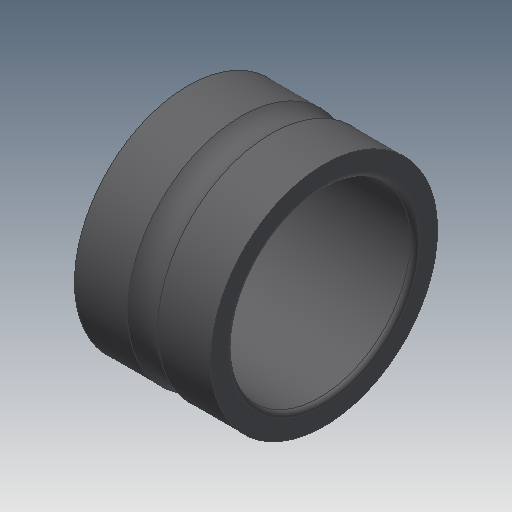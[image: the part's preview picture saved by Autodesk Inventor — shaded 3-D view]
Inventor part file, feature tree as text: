
AUTODESK INVENTOR PART (.ipt)
format: ipt  version: 2019.4 (Build 234330000, 330)  size: 198,656 bytes
history: native  units: mm
features: other x98, revolve x1, sketch x1
ambient origin geometry x8: Origin, YZ Plane, XZ Plane, XY Plane, X Axis, Y Axis, Z Axis, Center Point
bodies: Solid1 (feature_tree)
feature tree (100):
  revolve  "Revolution1"  [1 undecoded]
  other  "ip_st_1_1_XY"
  other  "ip_st_1_1_YZ"
  other  "ip_st_1_1_ZX"
  other  "ip_st_1_1_X"
  other  "ip_st_1_1_Y"
  other  "ip_st_1_1_Z"
  other  "ip_st_1_1_Center"
  other  "ip_st_1_10_XY"
  other  "ip_st_1_10_YZ"
  other  "ip_st_1_10_ZX"
  other  "ip_st_1_10_X"
  other  "ip_st_1_10_Y"
  other  "ip_st_1_10_Z"
  other  "ip_st_1_10_Center"
  other  "ip_st_1_11_XY"
  other  "ip_st_1_11_YZ"
  other  "ip_st_1_11_ZX"
  other  "ip_st_1_11_X"
  other  "ip_st_1_11_Y"
  other  "ip_st_1_11_Z"
  other  "ip_st_1_11_Center"
  other  "ip_st_1_12_XY"
  other  "ip_st_1_12_YZ"
  other  "ip_st_1_12_ZX"
  other  "ip_st_1_12_X"
  other  "ip_st_1_12_Y"
  other  "ip_st_1_12_Z"
  other  "ip_st_1_12_Center"
  other  "ip_st_1_2_XY"
  other  "ip_st_1_2_YZ"
  other  "ip_st_1_2_ZX"
  other  "ip_st_1_2_X"
  other  "ip_st_1_2_Y"
  other  "ip_st_1_2_Z"
  other  "ip_st_1_2_Center"
  other  "ip_st_1_3_XY"
  other  "ip_st_1_3_YZ"
  other  "ip_st_1_3_ZX"
  other  "ip_st_1_3_X"
  other  "ip_st_1_3_Y"
  other  "ip_st_1_3_Z"
  other  "ip_st_1_3_Center"
  other  "ip_st_1_4_XY"
  other  "ip_st_1_4_YZ"
  other  "ip_st_1_4_ZX"
  other  "ip_st_1_4_X"
  other  "ip_st_1_4_Y"
  other  "ip_st_1_4_Z"
  other  "ip_st_1_4_Center"
  other  "ip_st_1_5_XY"
  other  "ip_st_1_5_YZ"
  other  "ip_st_1_5_ZX"
  other  "ip_st_1_5_X"
  other  "ip_st_1_5_Y"
  other  "ip_st_1_5_Z"
  other  "ip_st_1_5_Center"
  other  "ip_st_1_6_XY"
  other  "ip_st_1_6_YZ"
  other  "ip_st_1_6_ZX"
  other  "ip_st_1_6_X"
  other  "ip_st_1_6_Y"
  other  "ip_st_1_6_Z"
  other  "ip_st_1_6_Center"
  other  "ip_st_1_7_XY"
  other  "ip_st_1_7_YZ"
  other  "ip_st_1_7_ZX"
  other  "ip_st_1_7_X"
  other  "ip_st_1_7_Y"
  other  "ip_st_1_7_Z"
  other  "ip_st_1_7_Center"
  other  "ip_st_1_8_XY"
  other  "ip_st_1_8_YZ"
  other  "ip_st_1_8_ZX"
  other  "ip_st_1_8_X"
  other  "ip_st_1_8_Y"
  other  "ip_st_1_8_Z"
  other  "ip_st_1_8_Center"
  other  "ip_st_1_9_XY"
  other  "ip_st_1_9_YZ"
  other  "ip_st_1_9_ZX"
  other  "ip_st_1_9_X"
  other  "ip_st_1_9_Y"
  other  "ip_st_1_9_Z"
  other  "ip_st_1_9_Center"
  other  "ip_st_1a_XY"
  other  "ip_st_1a_YZ"
  other  "ip_st_1a_ZX"
  other  "ip_st_1a_X"
  other  "ip_st_1a_Y"
  other  "ip_st_1a_Z"
  other  "ip_st_1a_Center"
  other  "ip_st_2a_XY"
  other  "ip_st_2a_YZ"
  other  "ip_st_2a_ZX"
  other  "ip_st_2a_X"
  other  "ip_st_2a_Y"
  other  "ip_st_2a_Z"
  other  "ip_st_2a_Center"
  sketch  "Sketch_1"  dims[d0=360.0deg d1=0.0mm]
note: 1 required parameter value undecoded (feature->parameter linkage not recoverable at this tier; creation-order binding heuristic only, values carry confidence <= 0.55)
